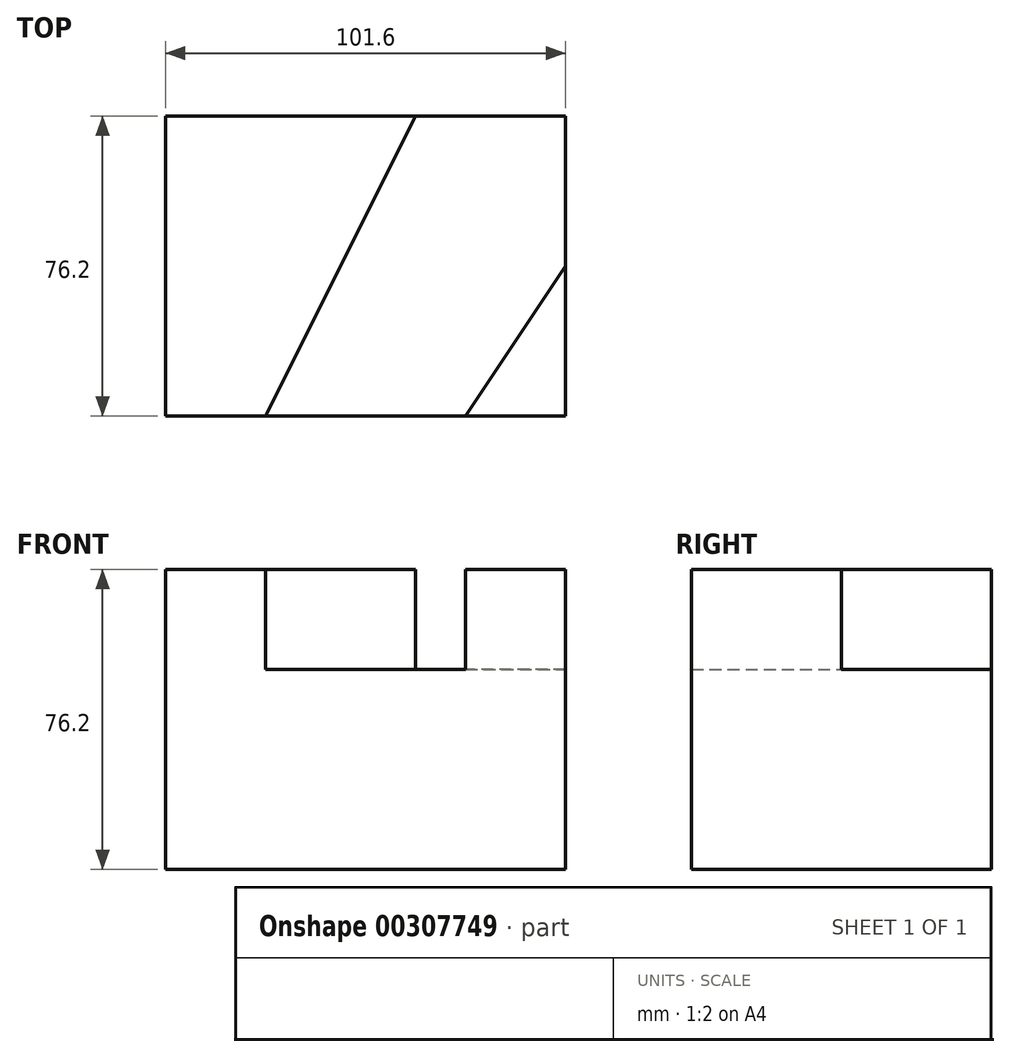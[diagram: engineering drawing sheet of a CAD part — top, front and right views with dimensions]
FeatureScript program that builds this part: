
annotation { "Feature Type Name" : "Feature", "Feature Type Description" : "" }
export const myFeature = defineFeature(function(context is Context, id is Id, definition is map)
    precondition{}
    {
        {
            var Q0;
            Q0=qCreatedBy(makeId("Front.planeOp"),FACE);
            var sketch = newSketch(context, id + "F0", { "sketchPlane" : qUnion([Q0])});
            skLineSegment(sketch, "E0", {"start": v(-45.98, -55.38) * mm, "end": v(55.62, -55.38) * mm});
            skLineSegment(sketch, "E1", {"start": v(55.62, -55.38) * mm, "end": v(55.62, -4.58) * mm});
            skLineSegment(sketch, "E2", {"start": v(55.62, -4.58) * mm, "end": v(-45.98, -4.58) * mm});
            skLineSegment(sketch, "E3", {"start": v(-45.98, -4.58) * mm, "end": v(-45.98, -55.38) * mm});
            skSolve(sketch);
        }
        {
            var Q0;
            Q0=makeQuery(id+"F0.imprint","IMPRINT",FACE,{"disambiguationData":[TD([[makeQuery(id+"F0.imprint","IMPRINT",EDGE,{"derivedFrom":sQuery(id+"F0.wireOp",EDGE,"E0")}),1.0]])]});
            extrude(context, id + "F1", {"entities" : qUnion([Q0]), "depth" : 76.2 * mm});
        }
        {
            var Q0;
            Q0=makeQuery(id+"F1.opExtrude","SWEPT_FACE",FACE,{"disambiguationData":[OSD([sQuery(id+"F0.wireOp",EDGE,"E2")])]});
            var sketch = newSketch(context, id + "F2", { "sketchPlane" : qUnion([Q0])});
            skLineSegment(sketch, "E4", {"start": v(55.62, -76.2) * mm, "end": v(30.22, -76.2) * mm});
            skLineSegment(sketch, "E5", {"start": v(55.62, -76.2) * mm, "end": v(55.62, -38.1) * mm});
            skLineSegment(sketch, "E6", {"start": v(30.22, -76.2) * mm, "end": v(55.62, -38.1) * mm});
            skSolve(sketch);
        }
        {
            var Q0;
            Q0 = qSketchRegion(id + "F2", true);
            extrude(context, id + "F3", {"entities" : qUnion([Q0]), "operationType" : NewBodyOperationType.ADD, "depth" : 25.4 * mm});
        }
        {
            var Q0;
            Q0=makeQuery(id+"F1.opExtrude","SWEPT_FACE",FACE,{"disambiguationData":[OSD([sQuery(id+"F0.wireOp",EDGE,"E2")])]});
            var sketch = newSketch(context, id + "F4", { "sketchPlane" : qUnion([Q0])});
            skLineSegment(sketch, "E7", {"start": v(-45.98, -76.2) * mm, "end": v(-45.98, 0) * mm});
            skLineSegment(sketch, "E8", {"start": v(-45.98, 0) * mm, "end": v(17.52, 0) * mm});
            skLineSegment(sketch, "E9", {"start": v(-45.98, -76.2) * mm, "end": v(-20.58, -76.2) * mm});
            skLineSegment(sketch, "E10", {"start": v(-20.58, -76.2) * mm, "end": v(17.52, 0) * mm});
            skSolve(sketch);
        }
        {
            var Q0;
            Q0 = qSketchRegion(id + "F4", true);
            extrude(context, id + "F5", {"entities" : qUnion([Q0]), "operationType" : NewBodyOperationType.ADD, "depth" : 25.4 * mm});
        }
    });
